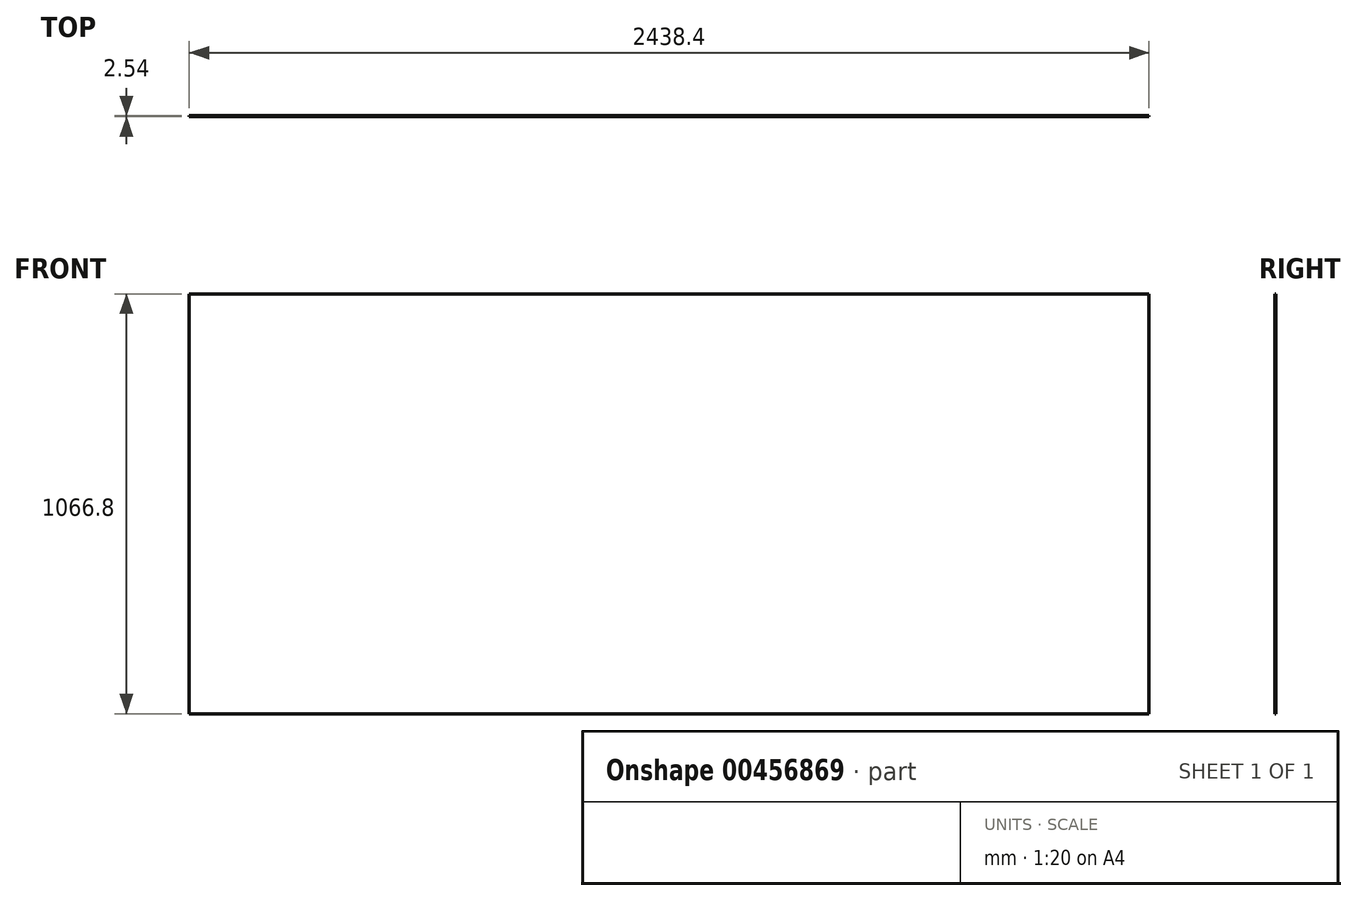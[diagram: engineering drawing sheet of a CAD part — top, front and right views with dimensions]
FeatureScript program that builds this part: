
annotation { "Feature Type Name" : "Feature", "Feature Type Description" : "" }
export const myFeature = defineFeature(function(context is Context, id is Id, definition is map)
    precondition{}
    {
        {
            var Q0;
            Q0=qCreatedBy(makeId("Front.planeOp"),FACE);
            var sketch = newSketch(context, id + "F0", { "sketchPlane" : qUnion([Q0])});
            skLineSegment(sketch, "E0.bottom", {"start": v(-1199.1, 359.98) * mm, "end": v(1239.3, 359.98) * mm});
            skLineSegment(sketch, "E0.top", {"start": v(-1199.1, -706.82) * mm, "end": v(1239.3, -706.82) * mm});
            skLineSegment(sketch, "E0.left", {"start": v(-1199.1, 359.98) * mm, "end": v(-1199.1, -706.82) * mm});
            skLineSegment(sketch, "E0.right", {"start": v(1239.3, 359.98) * mm, "end": v(1239.3, -706.82) * mm});
            skSolve(sketch);
        }
        {
            var Q0;
            Q0=makeQuery(id+"F0.imprint","IMPRINT",FACE,{"disambiguationData":[TD([[makeQuery(id+"F0.imprint","IMPRINT",EDGE,{"derivedFrom":sQuery(id+"F0.wireOp",EDGE,"E0.bottom")}),-1.0]])]});
            extrude(context, id + "F1", {"entities" : qUnion([Q0]), "depth" : 2.54 * mm});
        }
    });
